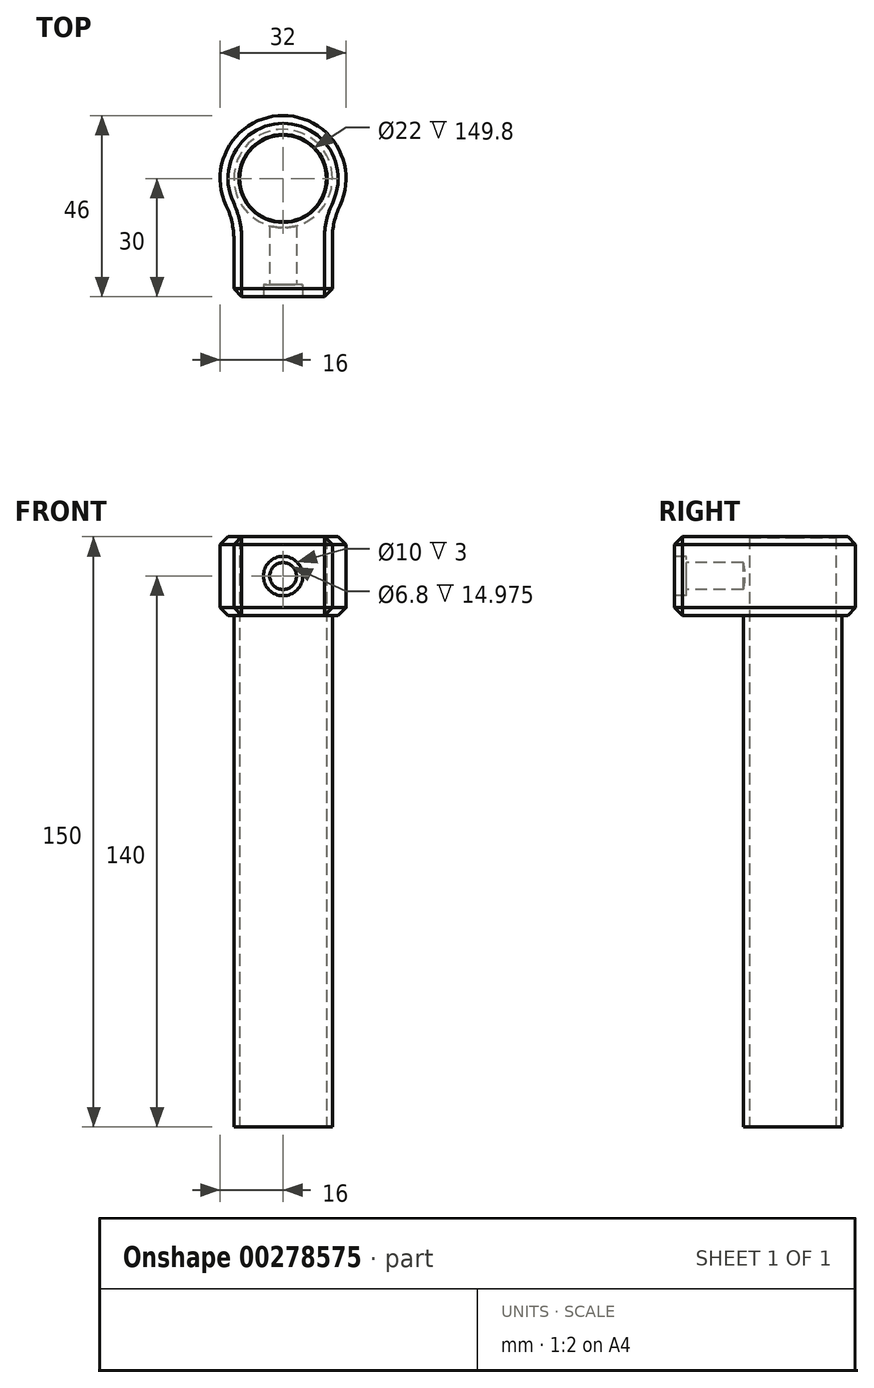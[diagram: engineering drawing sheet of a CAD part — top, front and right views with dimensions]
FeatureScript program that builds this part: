
annotation { "Feature Type Name" : "Feature", "Feature Type Description" : "" }
export const myFeature = defineFeature(function(context is Context, id is Id, definition is map)
    precondition{}
    {
        {
            var Q0;
            Q0=qCreatedBy(makeId("Top.planeOp"),FACE);
            var sketch = newSketch(context, id + "F0", { "sketchPlane" : qUnion([Q0])});
            skLineSegment(sketch, "E0.bottom", {"start": v(12.5, -15) * mm, "end": v(-12.5, -15) * mm});
            skLineSegment(sketch, "E0.top", {"start": v(12.5, 15) * mm, "end": v(-12.5, 15) * mm});
            skLineSegment(sketch, "E0.left", {"start": v(12.5, -15) * mm, "end": v(12.5, 15) * mm});
            skLineSegment(sketch, "E0.right", {"start": v(-12.5, -15) * mm, "end": v(-12.5, 15) * mm});
            skPoint(sketch, "E0.middle", {"position": v(0, 0) * mm});
            skCircle(sketch, "E1", {"center": v(0, 15) * mm, "radius": 12.5 * mm});
            skCircle(sketch, "E2", {"center": v(0, 15) * mm, "radius": 16 * mm});
            skCircle(sketch, "E3", {"center": v(0, 15) * mm, "radius": 11 * mm});
            skCircle(sketch, "E4", {"center": v(0, 15) * mm, "radius": 15 * mm});
            skCircle(sketch, "E5", {"center": v(0, 15) * mm, "radius": 10 * mm});
            skSolve(sketch);
        }
        {
            var Q0;
            {var subQ0=sQuery(id+"F0.wireOp",EDGE,"E0.bottom");Q0=makeQuery(id+"F0.imprint","IMPRINT",FACE,{"disambiguationData":[TD([[makeQuery(id+"F0.imprint","IMPRINT",EDGE,{"derivedFrom":subQ0}),-1.0]])]});}
            var Q1;
            {var subQ1=sQuery(id+"F0.wireOp",EDGE,"E0.left");var subQ4=sQuery(id+"F0.wireOp",EDGE,"E2");var subQ5=makeQuery(id+"F0.imprint","INTERSECT",VERTEX,{"derivedFrom":[subQ1,subQ4]});Q1=makeQuery(id+"F0.imprint","IMPRINT",FACE,{"disambiguationData":[TD([[makeQuery(id+"F0.imprint","IMPRINT",EDGE,{"disambiguationData":[TD([[subQ5,-1.0]])],"derivedFrom":subQ4}),1.0]])]});}
            var Q2;
            {var subQ1=sQuery(id+"F0.wireOp",EDGE,"E0.left");var subQ4=sQuery(id+"F0.wireOp",EDGE,"E2");var subQ5=makeQuery(id+"F0.imprint","INTERSECT",VERTEX,{"derivedFrom":[subQ1,subQ4]});Q2=makeQuery(id+"F0.imprint","IMPRINT",FACE,{"disambiguationData":[TD([[makeQuery(id+"F0.imprint","IMPRINT",EDGE,{"disambiguationData":[TD([[subQ5,1.0]])],"derivedFrom":subQ4}),1.0]])]});}
            var Q3;
            {var subQ1=sQuery(id+"F0.wireOp",EDGE,"E0.left");var subQ4=sQuery(id+"F0.wireOp",EDGE,"E4");var subQ5=makeQuery(id+"F0.imprint","INTERSECT",VERTEX,{"derivedFrom":[subQ1,subQ4]});Q3=makeQuery(id+"F0.imprint","IMPRINT",FACE,{"disambiguationData":[TD([[makeQuery(id+"F0.imprint","IMPRINT",EDGE,{"disambiguationData":[TD([[subQ5,1.0]])],"derivedFrom":subQ4}),1.0]])]});}
            var Q4;
            {var subQ1=sQuery(id+"F0.wireOp",EDGE,"E0.top");var subQ3=sQuery(id+"F0.wireOp",EDGE,"E3");var subQ4=makeQuery(id+"F0.imprint","INTERSECT",VERTEX,{"disambiguationData":[OD(0.0)],"derivedFrom":[subQ1,subQ3]});Q4=makeQuery(id+"F0.imprint","IMPRINT",FACE,{"disambiguationData":[TD([[makeQuery(id+"F0.imprint","IMPRINT",EDGE,{"disambiguationData":[TD([[subQ4,-1.0]])],"derivedFrom":subQ3}),-1.0]])]});}
            var Q5;
            {var subQ1=sQuery(id+"F0.wireOp",EDGE,"E0.top");var subQ3=sQuery(id+"F0.wireOp",EDGE,"E3");var subQ4=makeQuery(id+"F0.imprint","INTERSECT",VERTEX,{"disambiguationData":[OD(0.0)],"derivedFrom":[subQ1,subQ3]});Q5=makeQuery(id+"F0.imprint","IMPRINT",FACE,{"disambiguationData":[TD([[makeQuery(id+"F0.imprint","IMPRINT",EDGE,{"disambiguationData":[TD([[subQ4,1.0]])],"derivedFrom":subQ3}),-1.0]])]});}
            var Q6;
            {var subQ1=sQuery(id+"F0.wireOp",EDGE,"E0.left");var subQ4=sQuery(id+"F0.wireOp",EDGE,"E4");var subQ5=makeQuery(id+"F0.imprint","INTERSECT",VERTEX,{"derivedFrom":[subQ1,subQ4]});Q6=makeQuery(id+"F0.imprint","IMPRINT",FACE,{"disambiguationData":[TD([[makeQuery(id+"F0.imprint","IMPRINT",EDGE,{"disambiguationData":[TD([[subQ5,-1.0]])],"derivedFrom":subQ4}),1.0]])]});}
            var Q7;
            {var subQ1=sQuery(id+"F0.wireOp",EDGE,"E0.top");var subQ3=sQuery(id+"F0.wireOp",EDGE,"E3");var subQ4=makeQuery(id+"F0.imprint","INTERSECT",VERTEX,{"disambiguationData":[OD(0.0)],"derivedFrom":[subQ1,subQ3]});Q7=makeQuery(id+"F0.imprint","IMPRINT",FACE,{"disambiguationData":[TD([[makeQuery(id+"F0.imprint","IMPRINT",EDGE,{"disambiguationData":[TD([[subQ4,-1.0]])],"derivedFrom":subQ3}),-1.0]])]});}
            var Q8;
            {var subQ1=sQuery(id+"F0.wireOp",EDGE,"E0.top");var subQ3=sQuery(id+"F0.wireOp",EDGE,"E3");var subQ4=makeQuery(id+"F0.imprint","INTERSECT",VERTEX,{"disambiguationData":[OD(0.0)],"derivedFrom":[subQ1,subQ3]});Q8=makeQuery(id+"F0.imprint","IMPRINT",FACE,{"disambiguationData":[TD([[makeQuery(id+"F0.imprint","IMPRINT",EDGE,{"disambiguationData":[TD([[subQ4,1.0]])],"derivedFrom":subQ3}),-1.0]])]});}
            extrude(context, id + "F1", {"entities" : qUnion([Q0, Q1, Q2, Q3, Q4, Q5, Q6, Q7, Q8]), "depth" : 10 * mm, "hasSecondDirection" : true, "secondDirectionOppositeDirection" : true, "secondDirectionDepth" : 10 * mm});
        }
        {
            var Q0;
            Q0=makeQuery(id+"F1.opExtrude","SWEPT_EDGE",EDGE,{"disambiguationData":[OSD([sQuery(id+"F0.wireOp",EDGE,"E0.right"),sQuery(id+"F0.wireOp",EDGE,"E2")])]});
            var Q1;
            Q1=makeQuery(id+"F1.opExtrude","SWEPT_EDGE",EDGE,{"disambiguationData":[OSD([sQuery(id+"F0.wireOp",EDGE,"E0.left"),sQuery(id+"F0.wireOp",EDGE,"E2")])]});
            fillet(context, id + "F2", {"entities" : qUnion([Q0, Q1]), "radius" : 20 * mm, "tangentPropagation" : true, "allowEdgeOverflow" : false});
        }
        {
            var Q0;
            Q0=makeQuery(id+"F1.opExtrude","CAP_EDGE",EDGE,{"disambiguationData":[OSD([sQuery(id+"F0.wireOp",EDGE,"E0.right")])],"isStart":false});
            var Q1;
            Q1=makeQuery(id+"F1.opExtrude","CAP_EDGE",EDGE,{"disambiguationData":[OSD([sQuery(id+"F0.wireOp",EDGE,"E0.right")])],"isStart":true});
            var Q2;
            Q2=makeQuery(id+"F1.opExtrude","SWEPT_FACE",FACE,{"disambiguationData":[OSD([sQuery(id+"F0.wireOp",EDGE,"E0.bottom")])]});
            chamfer(context, id + "F3", {"entities" : qUnion([Q0, Q1, Q2]), "width" : 2 * mm, "tangentPropagation" : true});
        }
        {
            var Q0;
            Q0=makeQuery(id+"F1.opExtrude","CAP_EDGE",EDGE,{"disambiguationData":[OSD([sQuery(id+"F0.wireOp",EDGE,"E1")])],"isStart":false});
            var Q1;
            Q1=makeQuery(id+"F1.opExtrude","CAP_EDGE",EDGE,{"disambiguationData":[OSD([sQuery(id+"F0.wireOp",EDGE,"E1")])],"isStart":true});
            var Q2;
            Q2=makeQuery(id+"F1.opExtrude","CAP_EDGE",EDGE,{"disambiguationData":[OSD([sQuery(id+"F0.wireOp",EDGE,"E3")])],"isStart":false});
            var Q3;
            Q3=makeQuery(id+"F1.opExtrude","SWEPT_FACE",FACE,{"disambiguationData":[OSD([sQuery(id+"F0.wireOp",EDGE,"E3")])]});
            chamfer(context, id + "F4", {"entities" : qUnion([Q0, Q1, Q2, Q3]), "width" : 0.5 * mm, "tangentPropagation" : true});
        }
        {
            var Q0;
            Q0=makeQuery(id+"F1.opExtrude","SWEPT_FACE",FACE,{"disambiguationData":[OSD([sQuery(id+"F0.wireOp",EDGE,"E0.bottom")])]});
            var sketch = newSketch(context, id + "F5", { "sketchPlane" : qUnion([Q0])});
            skCircle(sketch, "E6", {"center": v(0, 0) * mm, "radius": 3.4 * mm});
            skCircle(sketch, "E7", {"center": v(0, 0) * mm, "radius": 5 * mm});
            skSolve(sketch);
        }
        {
            var Q0;
            Q0=makeQuery(id+"F5.imprint","IMPRINT",FACE,{"disambiguationData":[TD([[makeQuery(id+"F5.imprint","IMPRINT",EDGE,{"derivedFrom":sQuery(id+"F5.wireOp",EDGE,"E6")}),1.0]])]});
            extrude(context, id + "F6", {"entities" : qUnion([Q0]), "operationType" : NewBodyOperationType.REMOVE, "oppositeDirection" : true, "depth" : 18 * mm});
        }
        {
            var Q0;
            Q0=makeQuery(id+"F5.imprint","IMPRINT",FACE,{"disambiguationData":[TD([[makeQuery(id+"F5.imprint","IMPRINT",EDGE,{"derivedFrom":sQuery(id+"F5.wireOp",EDGE,"E6")}),-1.0]])]});
            var Q1;
            Q1 = qBodyType(qCreatedBy(id + "F5" ,EDGE), BodyType.WIRE);
            var Q2;
            Q2=sQuery(id+"F5.wireOp",EDGE,"E7");
            extrude(context, id + "F7", {"entities" : qUnion([Q0]), "operationType" : NewBodyOperationType.REMOVE, "surfaceEntities" : qUnion([Q1, Q2]), "oppositeDirection" : true, "depth" : 3 * mm});
        }
        {
            var Q0;
            {var subQ1=sQuery(id+"F0.wireOp",EDGE,"E0.top");var subQ3=sQuery(id+"F0.wireOp",EDGE,"E3");var subQ4=makeQuery(id+"F0.imprint","INTERSECT",VERTEX,{"disambiguationData":[OD(0.0)],"derivedFrom":[subQ1,subQ3]});Q0=makeQuery(id+"F0.imprint","IMPRINT",FACE,{"disambiguationData":[TD([[makeQuery(id+"F0.imprint","IMPRINT",EDGE,{"disambiguationData":[TD([[subQ4,-1.0]])],"derivedFrom":subQ3}),-1.0]])]});}
            var Q1;
            {var subQ1=sQuery(id+"F0.wireOp",EDGE,"E0.top");var subQ3=sQuery(id+"F0.wireOp",EDGE,"E3");var subQ4=makeQuery(id+"F0.imprint","INTERSECT",VERTEX,{"disambiguationData":[OD(0.0)],"derivedFrom":[subQ1,subQ3]});Q1=makeQuery(id+"F0.imprint","IMPRINT",FACE,{"disambiguationData":[TD([[makeQuery(id+"F0.imprint","IMPRINT",EDGE,{"disambiguationData":[TD([[subQ4,1.0]])],"derivedFrom":subQ3}),-1.0]])]});}
            var Q2;
            {var subQ0=sQuery(id+"F0.wireOp",EDGE,"E3");var subQ1=sQuery(id+"F0.wireOp",EDGE,"E0.top");var subQ2=makeQuery(id+"F0.imprint","INTERSECT",VERTEX,{"disambiguationData":[OD(0.0)],"derivedFrom":[subQ1,subQ0]});Q2=makeQuery(id+"F0.imprint","IMPRINT",FACE,{"disambiguationData":[TD([[makeQuery(id+"F0.imprint","IMPRINT",EDGE,{"disambiguationData":[TD([[subQ2,-1.0]])],"derivedFrom":subQ1}),-1.0]])]});}
            var Q3;
            {var subQ0=sQuery(id+"F0.wireOp",EDGE,"E3");var subQ1=sQuery(id+"F0.wireOp",EDGE,"E0.top");var subQ2=makeQuery(id+"F0.imprint","INTERSECT",VERTEX,{"disambiguationData":[OD(0.0)],"derivedFrom":[subQ1,subQ0]});Q3=makeQuery(id+"F0.imprint","IMPRINT",FACE,{"disambiguationData":[TD([[makeQuery(id+"F0.imprint","IMPRINT",EDGE,{"disambiguationData":[TD([[subQ2,-1.0]])],"derivedFrom":subQ1}),1.0]])]});}
            extrude(context, id + "F8", {"entities" : qUnion([Q0, Q1, Q2, Q3]), "oppositeDirection" : true, "depth" : 140 * mm, "hasSecondDirection" : true, "secondDirectionOppositeDirection" : false, "secondDirectionDepth" : 10 * mm});
        }
        {
            var Q0;
            {var subQ1=sQuery(id+"F0.wireOp",EDGE,"E0.top");var subQ3=sQuery(id+"F0.wireOp",EDGE,"E3");var subQ4=makeQuery(id+"F0.imprint","INTERSECT",VERTEX,{"disambiguationData":[OD(0.0)],"derivedFrom":[subQ1,subQ3]});Q0=makeQuery(id+"F0.imprint","IMPRINT",FACE,{"disambiguationData":[TD([[makeQuery(id+"F0.imprint","IMPRINT",EDGE,{"disambiguationData":[TD([[subQ4,1.0]])],"derivedFrom":subQ3}),-1.0]])]});}
            var Q1;
            {var subQ1=sQuery(id+"F0.wireOp",EDGE,"E0.top");var subQ3=sQuery(id+"F0.wireOp",EDGE,"E3");var subQ4=makeQuery(id+"F0.imprint","INTERSECT",VERTEX,{"disambiguationData":[OD(0.0)],"derivedFrom":[subQ1,subQ3]});Q1=makeQuery(id+"F0.imprint","IMPRINT",FACE,{"disambiguationData":[TD([[makeQuery(id+"F0.imprint","IMPRINT",EDGE,{"disambiguationData":[TD([[subQ4,-1.0]])],"derivedFrom":subQ3}),-1.0]])]});}
            extrude(context, id + "F9", {"entities" : qUnion([Q0, Q1]), "operationType" : NewBodyOperationType.ADD, "oppositeDirection" : true, "depth" : 140 * mm, "hasSecondDirection" : true, "secondDirectionOppositeDirection" : true, "secondDirectionDepth" : 10 * mm});
        }
        {
            var Q0;
            Q0=makeQuery(id+"F8.opExtrude","CAP_EDGE",EDGE,{"disambiguationData":[OSD([sQuery(id+"F0.wireOp",EDGE,"E5")])],"isStart":true});
            var Q1;
            Q1=makeQuery(id+"F8.opExtrude","CAP_EDGE",EDGE,{"disambiguationData":[OSD([sQuery(id+"F0.wireOp",EDGE,"E3")])],"isStart":true});
            var Q2;
            Q2=makeQuery(id+"F9.opExtrude","CAP_EDGE",EDGE,{"disambiguationData":[OSD([sQuery(id+"F0.wireOp",EDGE,"E1")])],"isStart":true});
            var Q3;
            Q3=makeQuery(id+"F9.opExtrude","CAP_EDGE",EDGE,{"disambiguationData":[OSD([sQuery(id+"F0.wireOp",EDGE,"E1")])],"isStart":false});
            var Q4;
            Q4=makeQuery(id+"F8.opExtrude","CAP_EDGE",EDGE,{"disambiguationData":[OSD([sQuery(id+"F0.wireOp",EDGE,"E5")])],"isStart":false});
            chamfer(context, id + "F10", {"entities" : qUnion([Q0, Q1, Q2, Q3, Q4]), "width" : 0.2 * mm, "tangentPropagation" : true});
        }
    });
